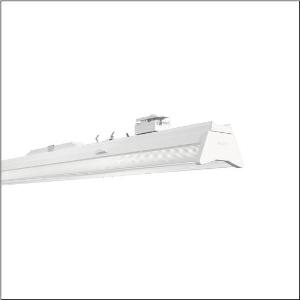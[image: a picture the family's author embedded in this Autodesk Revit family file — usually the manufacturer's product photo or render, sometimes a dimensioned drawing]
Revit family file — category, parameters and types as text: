
# Revit family: licross_r__11_performance_ho_51tm16mn4gxm_a288
name_source: partatom
category: Lighting Fixtures
units: mm (PartAtom-declared; Revit-internal decimal feet)

## family parameters
Cut with Voids When Loaded = No
Host = Face
Light Source = No
Part Type = Normal
Room Calculation Point = No
Round Connector Dimension = Use Diameter
Shared = No

## types (1)
- --- (1 x LED, 16020 lm, 87.4 W, 4000K)
    Apparent Load = 87 VA
    CIE Flux Codes = 63 87 95 78 100
    Color Rendering = 80
    Color Temperature = 4000K
    Default Elevation = 1800 mm
    Description = Licross® 11 Performance HO, luminaire insert, of sheet steel, galvanised, coil coated, white, length: 1.500mm, width: 120mm, height: 123mm, LED rated luminous flux: 16.020lm, light colour: 840, control gear: ON/OFF Multilumen, with plug, 3-pole, with phase selection, mains connection: 220..240V, AC, 50/60Hz, rated input power: 87W, halogen-free wiring, primary light control with lens, of plastic, primary optical cover: cover, of PMMA, light emission: direct/indirect distribution, primary light characteristic: symmetric, protection rating (complete): IP40, insulation class (complete): insulation class I (protective earthing), certification: CE, ENEC, VDE, UKCA, protection symbol: D if used in an environment without relevant dust loads with corresponding accessories, impact resistance: IK06, permissible ambient temperature for indoor applications: -35..+35°C, corresponds to IFS (International Featured Standards) requirements for safety and quality in the food industry, reducing of maximum allowable ambient temperature of 5°C with ceiling mounting, LABS conformity tested according to VDMA 24364:2018-05, packaging unit: 1 piece
    Height = 114 mm
    Lamp = 1 x LED
    Lamp Light Flux = 16020 lm
    Lamp Power = 87.4 W
    Lamp count = 1
    Length = 1500 mm
    Luminous efficacy = 183 lm/W
    Manufacturer = Siteco
    ModVariant = No
    Model = 51TM16MN4GXM
    Mounting Place = Ceiling
    Mounting Type = Pendant
    Number of Poles = 1
    OnlyDefault = Yes
    Power Factor = 1
    Product Name = Licross® 11 Performance HO
    Product group = luminaire insert
    ProductGroupID = 901
    Protection Class = Protection class I
    Protection Degree = IP 40
    RLX_Detail_Level = 1
    RLX_Emergency_Light_Flux = 0 lm
    RLX_Emergency_Type = 0
    RLX_Emergency_Type_DB = No
    RlxData = <blob elided: 31797 chars, md5=15f148ff>
    Socket = socket
    Standby Power = 0 W
    System Light Flux = 16020 lm
    System Power = 87 W
    Type Comments = factory setting: luminous flux: 100 % | (A | C | E) | 203 mA
    Type Image = l_1256138.jpg
    URL = http://relux.com
    VarID = @adj_055549
    Voltage = 0 V
    Weight = 0.00 kg
    Width = 120 mm

## geometry (parser evidence)
native form markers: Blend x4, Sweep x12
no freeform markers — native parametric forms only
